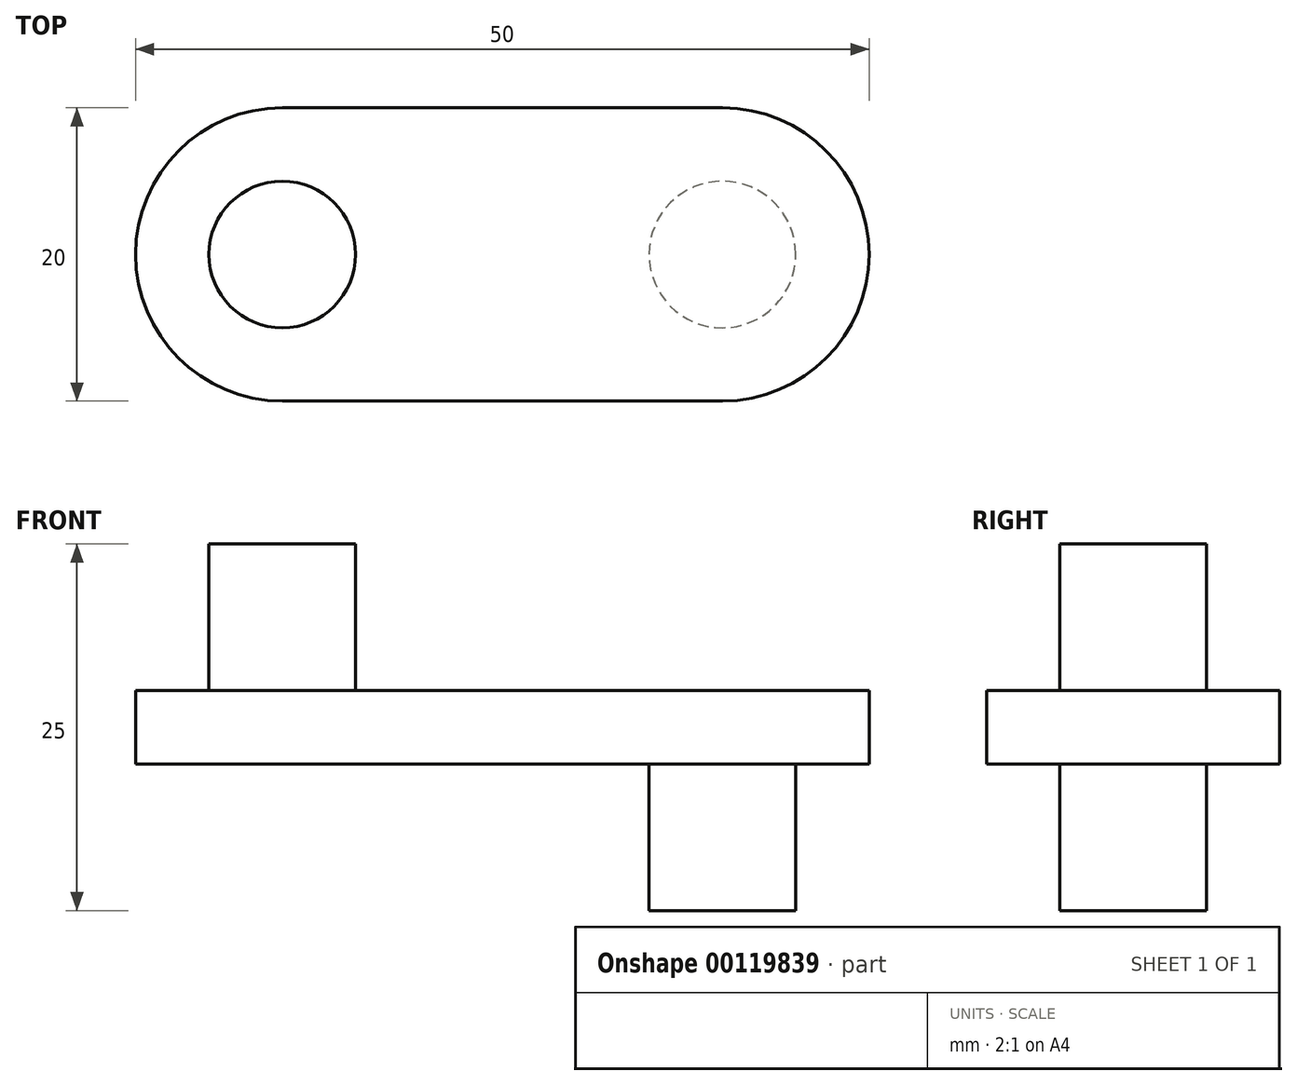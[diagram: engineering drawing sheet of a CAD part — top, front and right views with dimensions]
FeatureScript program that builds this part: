
annotation { "Feature Type Name" : "Feature", "Feature Type Description" : "" }
export const myFeature = defineFeature(function(context is Context, id is Id, definition is map)
    precondition{}
    {
        {
            var Q0;
            Q0=qCreatedBy(makeId("Top.planeOp"),FACE);
            var sketch = newSketch(context, id + "F0", { "sketchPlane" : qUnion([Q0])});
            skLineSegment(sketch, "E0.bottom", {"start": v(0, 0) * mm, "end": v(-30, 0) * mm});
            skLineSegment(sketch, "E0.top", {"start": v(0, 20) * mm, "end": v(-30, 20) * mm});
            skCircle(sketch, "E1", {"center": v(0, 10) * mm, "radius": 5 * mm});
            skCircle(sketch, "E2", {"center": v(-30, 10) * mm, "radius": 5 * mm});
            skArc(sketch, "E3", {"start": v(0, 20) * mm, "mid": v(10, 10) * mm, "end": v(0, 0) * mm});
            skArc(sketch, "E4", {"start": v(-30, 0) * mm, "mid": v(-40, 10) * mm, "end": v(-30, 20) * mm});
            skSolve(sketch);
        }
        {
            var Q0;
            Q0 = qSketchRegion(id + "F0", true);
            extrude(context, id + "F1", {"entities" : qUnion([Q0]), "depth" : 5 * mm});
        }
        {
            var Q0;
            Q0=qCreatedBy(makeId("Top.planeOp"),FACE);
            var sketch = newSketch(context, id + "F2", { "sketchPlane" : qUnion([Q0])});
            skCircle(sketch, "E5", {"center": v(-30, 10) * mm, "radius": 5 * mm});
            skSolve(sketch);
        }
        {
            var Q0;
            Q0 = qSketchRegion(id + "F2", true);
            extrude(context, id + "F3", {"entities" : qUnion([Q0]), "operationType" : NewBodyOperationType.ADD, "depth" : 15 * mm});
        }
        {
            var Q0;
            Q0=qCreatedBy(makeId("Top.planeOp"),FACE);
            var sketch = newSketch(context, id + "F4", { "sketchPlane" : qUnion([Q0])});
            skCircle(sketch, "E6", {"center": v(0, 10) * mm, "radius": 5 * mm});
            skSolve(sketch);
        }
        {
            var Q0;
            Q0 = qSketchRegion(id + "F4", true);
            extrude(context, id + "F5", {"entities" : qUnion([Q0]), "operationType" : NewBodyOperationType.ADD, "depth" : 5 * mm, "hasSecondDirection" : true, "secondDirectionOppositeDirection" : true, "secondDirectionDepth" : 10 * mm});
        }
    });
